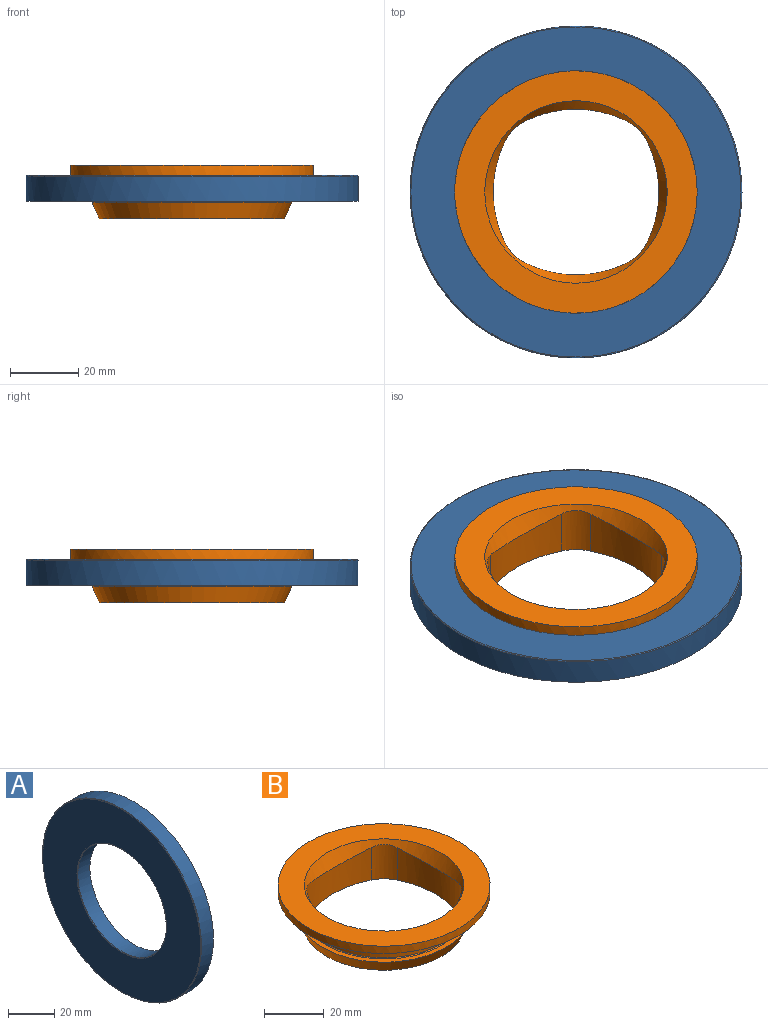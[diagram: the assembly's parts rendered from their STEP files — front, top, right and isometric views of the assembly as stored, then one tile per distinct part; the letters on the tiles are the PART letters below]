
ASSEMBLY  parts=2 mates=1
PART A: 12 faces, bbox 7.6x105x105 mm
  f0: plane 97.03x97.03mm, normal (1,0,0), area 230.5mm2, adj f1,f7
  f1: cylinder r=48.51mm len=97.03mm, axis (-1,0,0), area 2245.3mm2, adj f0,f8
  f2: plane 96.52x96.52mm, normal (-1,0,0), area 4974.6mm2, adj f8,f9
  f3: cylinder r=27.05mm len=54.1mm, axis (-1,0,0), area 1252mm2, adj f4,f9
  f4: plane 55.63x55.63mm, normal (1,0,0), area 131.3mm2, adj f3,f5
  f5: cylinder r=27.81mm len=55.63mm, axis (-1,0,0), area 1154.1mm2, adj f4,f10
  f6: plane 95x95mm, normal (1,0,0), area 4612.8mm2, adj f10,f11
  f7: cylinder r=47.75mm len=95.5mm, axis (-1,0,0), area 1981.4mm2, adj f0,f11
  f8: torus R=48.26mm, axis (1,0,0), area 121.4mm2, adj f1,f2
  f9: torus R=27.3mm, axis (1,0,0), area 68mm2, adj f2,f3
  f10: torus R=28.07mm, axis (-1,0,0), area 70mm2, adj f5,f6
  f11: torus R=47.5mm, axis (-1,0,0), area 119.5mm2, adj f6,f7
PART B: 18 faces, bbox 70.9x70.9x15.7 mm
  f0: plane 54.1x54.1mm, normal (0,0,-1), area 353.5mm2, adj f1,f2,f3,f4,f5,f6,f7,f8
  f1: cylinder r=12.7mm len=14.05mm, axis (0,0,1), area 122.1mm2, adj f0,f2,f8,f11
  f2: cylinder r=33.53mm len=29.36mm, axis (0,0,1), area 346.5mm2, adj f0,f1,f3,f11
  f3: cylinder r=12.7mm len=14.05mm, axis (0,0,1), area 122.1mm2, adj f0,f2,f4,f11
  f4: cylinder r=33.53mm len=29.36mm, axis (0,0,1), area 346.5mm2, adj f0,f3,f5,f11
  f5: cylinder r=12.7mm len=14.05mm, axis (0,0,1), area 122.1mm2, adj f0,f4,f6,f11
  f6: cylinder r=33.53mm len=29.36mm, axis (0,0,1), area 346.5mm2, adj f0,f5,f7,f11
  f7: cylinder r=12.7mm len=14.05mm, axis (0,0,1), area 122.1mm2, adj f0,f6,f8,f11
  f8: cylinder r=33.53mm len=29.36mm, axis (0,0,1), area 346.5mm2, adj f0,f1,f7,f11
  f9: cylinder r=35.43mm len=70.87mm, axis (0,0,1), area 667.9mm2, adj f10,f12
  f10: plane 70.87x70.87mm, normal (0,0,1), area 1709.7mm2, adj f9,f11
  f11: cone r=23.12mm half-angle=25deg, axis (0,0,1), area 684.2mm2, adj f1,f2,f3,f4,f5,f6,f7,f8
  f12: plane 70.87x70.87mm, normal (0,0,-1), area 1594.1mm2, adj f9,f16
  f13: cylinder r=27.05mm len=54.1mm, axis (0,0,-1), area 1244.2mm2, adj f16,f17
  f14: plane 58.42x58.42mm, normal (0,0,1), area 330.3mm2, adj f15,f17
  f15: cone r=29.21mm half-angle=24.1deg, axis (0,0,1), area 934.8mm2, adj f0,f14
  f16: torus R=27.35mm, axis (0,0,1), area 80.4mm2, adj f12,f13
  f17: torus R=27.35mm, axis (0,0,-1), area 80.4mm2, adj f13,f14
PLACE A rot(axis=(0,1,0),90deg) t=(0,0,-3)mm
PLACE B at identity
MATE fastened A.f1 <-> B.f11  axis (0,0,1) through (0,0,-3)mm
